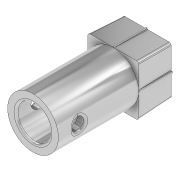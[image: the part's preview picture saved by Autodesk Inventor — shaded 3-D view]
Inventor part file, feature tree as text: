
AUTODESK INVENTOR PART (.ipt)
format: ipt  version: 2020 (Build 240168000, 168)  size: 290,304 bytes
history: native  units: in
note: dims shown in document units (in); Inventor stores cm internally (conversion verified against a paired STEP export)
features: extrude x6, fillet x5, sketch x5, projected_geometry x5, chamfer x4
ambient origin geometry x8: Origin, YZ Plane, XZ Plane, XY Plane, X Axis, Y Axis, Z Axis, Center Point
bodies: Solid1 (feature_tree)
feature tree (25):
  extrude  "Extrusion1"  Depth=0.315in
  extrude  "Extrusion2"  Depth=0.315in TaperAngle=0.0deg
  chamfer  "Chamfer1"  Distance=0.315in
  extrude  "Extrusion3"  Depth=0.0197in TaperAngle=0.0deg
  extrude  "Extrusion4"  Depth=0.3937in TaperAngle=0.0deg
  extrude  "Extrusion5"  Depth=0.0079in TaperAngle=0.0deg
  chamfer  "Chamfer2"  Distance=0.315in
  chamfer  "Chamfer3"  Distance=0.1969in
  chamfer  "Chamfer4"  Distance=0.315in
  fillet  "Fillet1"  Radius=0.315in
  fillet  "Fillet2"  Radius=0.315in
  fillet  "Fillet3"  Radius=0.0197in
  fillet  "Fillet4"  Radius=0.0197in
  extrude  "Extrusion6"  Depth=0.0079in
  fillet  "Fillet5"  Radius=0.0197in
  sketch  "Sketch1"  dims[d0=0.4724in d1=0.315in]
  sketch  "Sketch2"  dims[d2=0.3346in d3=0.0in d10=0.315in d11=0.0in d12=0.315in d13=0.125in d14=0.0137in]
  sketch  "Sketch3"  dims[d15=0.4724in d16=0.0197in d17=0.0in]
  sketch  "Sketch4"  dims[d18=0.4724in d19=0.3937in d20=0.0in]
  sketch  "Sketch6"  dims[d21=0.1181in d22=0.197in d23=0.0in d24=0.315in d25=0.1969in d26=0.315in d27=0.125in d28=0.0137in d29=0.315in d30=0.125in d31=0.0137in d32=0.315in d33=0.125in d34=0.0137in d35=0.0197in d36=0.0197in d37=0.0197in d38=0.0197in d39=0.0157in d40=1.5748in d42=360.0deg d44=0.315in d45=0.0in d46=0.0079in]
  projected_geometry  "Projected Loop2"
  projected_geometry  "Projected Loop3"
  projected_geometry  "Projected Loop4"
  projected_geometry  "Projected Loop5"
  projected_geometry  "Projected Loop6"
